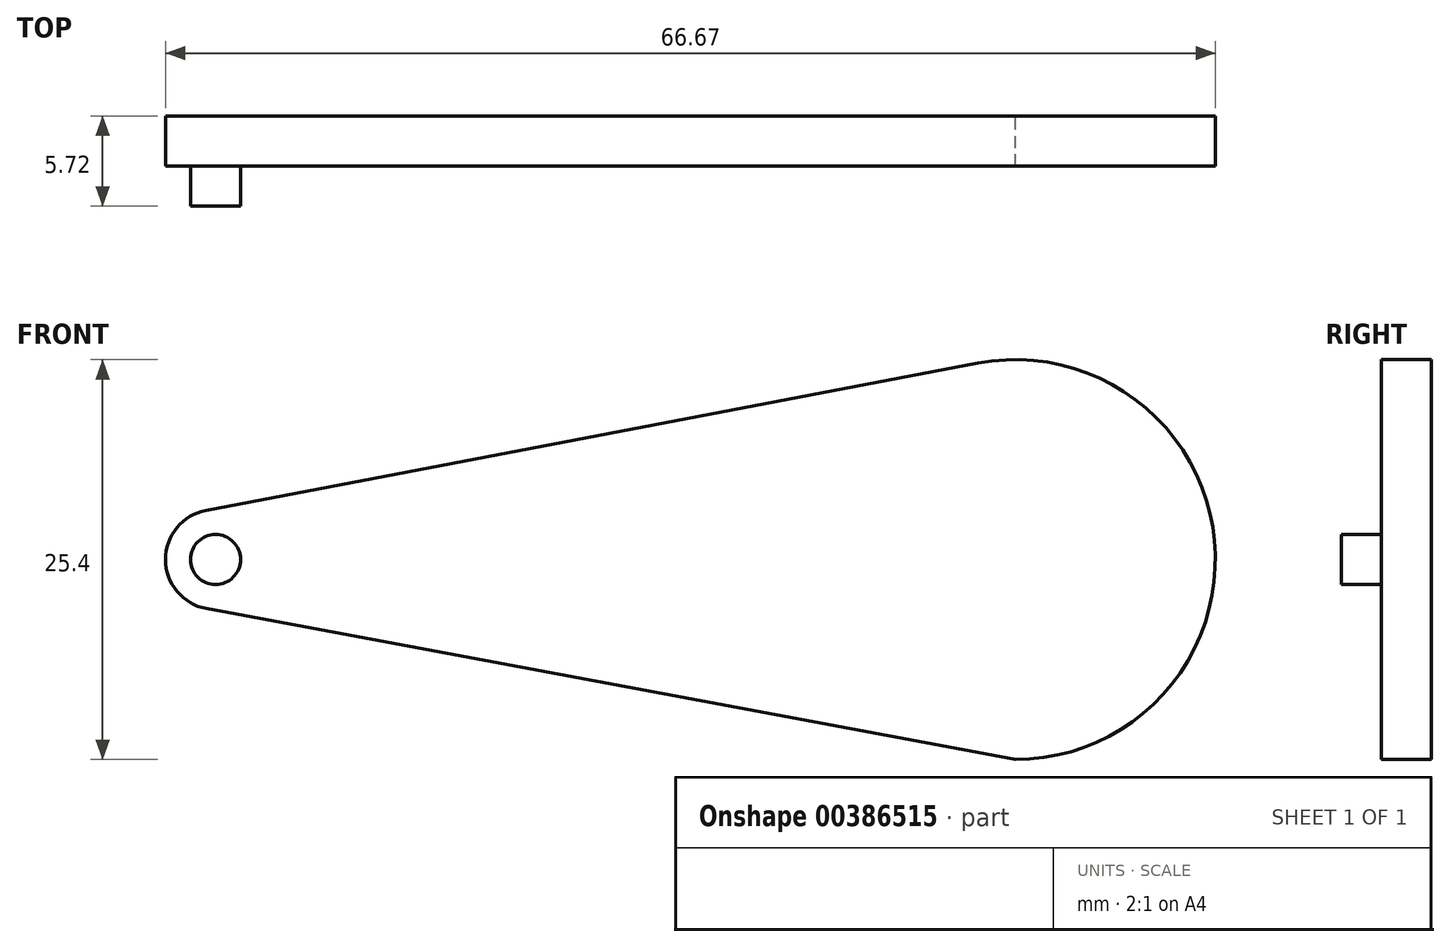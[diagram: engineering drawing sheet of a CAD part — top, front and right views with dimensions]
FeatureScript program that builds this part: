
annotation { "Feature Type Name" : "Feature", "Feature Type Description" : "" }
export const myFeature = defineFeature(function(context is Context, id is Id, definition is map)
    precondition{}
    {
        {
            var Q0;
            Q0=qCreatedBy(makeId("Front.planeOp"),FACE);
            var sketch = newSketch(context, id + "F0", { "sketchPlane" : qUnion([Q0])});
            skArc(sketch, "E0", {"start": v(-4.58, -11.85) * mm, "mid": v(12.65, -1.14) * mm, "end": v(-2.38, 12.47) * mm});
            skArc(sketch, "E1", {"start": v(-51.4, 3.12) * mm, "mid": v(-53.97, 0) * mm, "end": v(-51.38, -3.12) * mm});
            skLineSegment(sketch, "E2", {"start": v(-51.4, 3.12) * mm, "end": v(-2.38, 12.47) * mm});
            skLineSegment(sketch, "E3", {"start": v(-51.38, -3.12) * mm, "end": v(0, -12.7) * mm});
            skSolve(sketch);
        }
        {
            var Q0;
            {var subQ3=sQuery(id+"F0.wireOp",EDGE,"E1");Q0=makeQuery(id+"F0.imprint","IMPRINT",FACE,{"disambiguationData":[TD([[makeQuery(id+"F0.imprint","IMPRINT",EDGE,{"derivedFrom":subQ3}),1.0]])]});}
            extrude(context, id + "F1", {"entities" : qUnion([Q0]), "depth" : 3.17 * mm});
        }
        {
            var Q0;
            Q0=makeQuery(id+"F1.opExtrude","CAP_FACE",FACE,{"disambiguationData":[OSD([sQuery(id+"F0.wireOp",EDGE,"E0"),sQuery(id+"F0.wireOp",EDGE,"E1"),sQuery(id+"F0.wireOp",EDGE,"E2"),sQuery(id+"F0.wireOp",EDGE,"E3")])],"isStart":false});
            var sketch = newSketch(context, id + "F2", { "sketchPlane" : qUnion([Q0])});
            skPoint(sketch, "E4", {"position": v(-50.8, 0) * mm});
            skCircle(sketch, "E5", {"center": v(-50.8, 0) * mm, "radius": 1.59 * mm});
            skSolve(sketch);
        }
        {
            var Q0;
            Q0=makeQuery(id+"F2.imprint","IMPRINT",FACE,{"disambiguationData":[TD([[makeQuery(id+"F2.imprint","IMPRINT",EDGE,{"derivedFrom":sQuery(id+"F2.wireOp",EDGE,"E5")}),1.0]])]});
            extrude(context, id + "F3", {"entities" : qUnion([Q0]), "operationType" : NewBodyOperationType.ADD, "depth" : 2.54 * mm});
        }
    });
